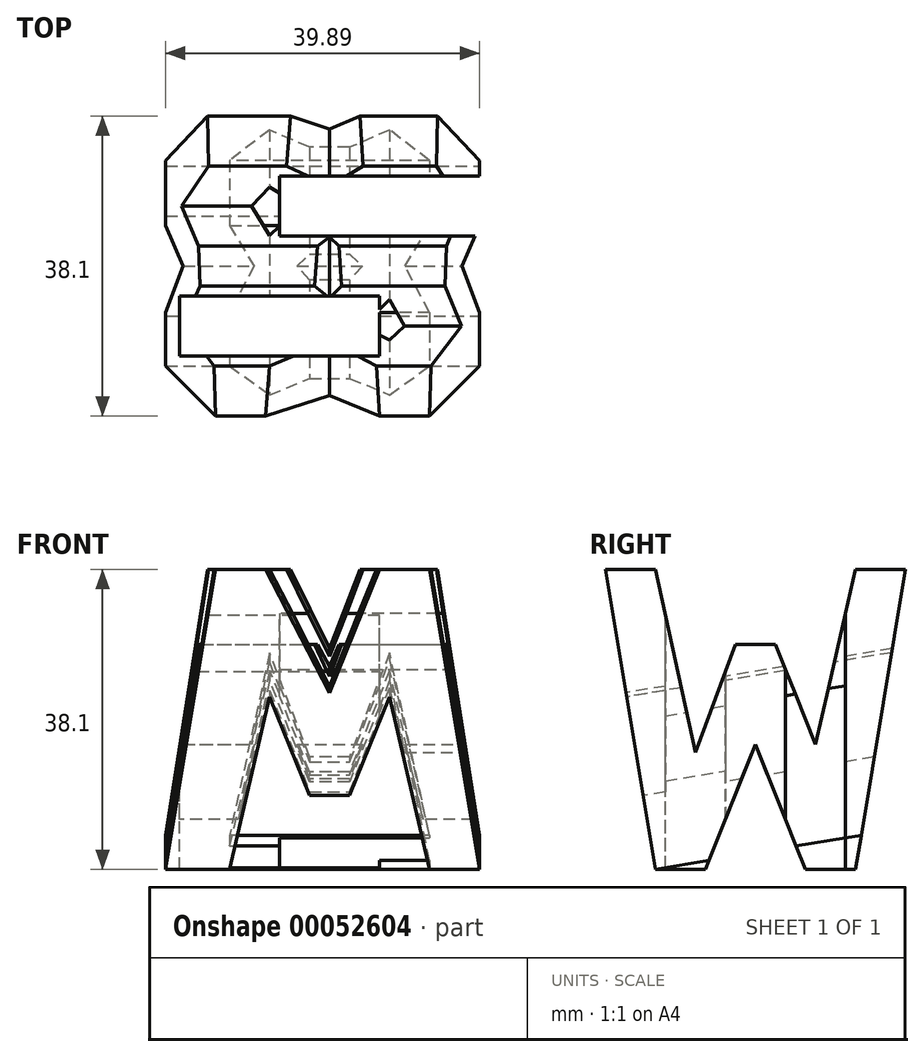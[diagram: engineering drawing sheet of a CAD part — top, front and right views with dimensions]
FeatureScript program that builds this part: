
annotation { "Feature Type Name" : "Feature", "Feature Type Description" : "" }
export const myFeature = defineFeature(function(context is Context, id is Id, definition is map)
    precondition{}
    {
        {
            var Q0;
            Q0=qCreatedBy(makeId("Front.planeOp"),FACE);
            var sketch = newSketch(context, id + "F0", { "sketchPlane" : qUnion([Q0])});
            skLineSegment(sketch, "E0", {"start": v(0, 0) * mm, "end": v(0, 38.1) * mm});
            skLineSegment(sketch, "E1", {"start": v(0, 38.1) * mm, "end": v(-39.89, 38.1) * mm});
            skLineSegment(sketch, "E2", {"start": v(-39.89, 38.1) * mm, "end": v(-39.89, 0) * mm});
            skLineSegment(sketch, "E3", {"start": v(-39.89, 0) * mm, "end": v(0, 0) * mm});
            skSolve(sketch);
        }
        {
            var Q0;
            Q0=makeQuery(id+"F0.imprint","IMPRINT",FACE,{"disambiguationData":[TD([[makeQuery(id+"F0.imprint","IMPRINT",EDGE,{"derivedFrom":sQuery(id+"F0.wireOp",EDGE,"E0")}),1.0]])]});
            extrude(context, id + "F1", {"entities" : qUnion([Q0]), "depth" : 38.1 * mm});
        }
        {
            var Q0;
            Q0=makeQuery(id+"F1.opExtrude","SWEPT_FACE",FACE,{"disambiguationData":[OSD([sQuery(id+"F0.wireOp",EDGE,"E0")])]});
            var sketch = newSketch(context, id + "F2", { "sketchPlane" : qUnion([Q0])});
            skLineSegment(sketch, "E4", {"start": v(-38.1, 38.1) * mm, "end": v(-31.75, 0) * mm});
            skLineSegment(sketch, "E5", {"start": v(-31.75, 0) * mm, "end": v(-25.4, 0) * mm});
            skLineSegment(sketch, "E6", {"start": v(-25.4, 0) * mm, "end": v(-19.05, 15.88) * mm});
            skLineSegment(sketch, "E7", {"start": v(-19.05, 15.88) * mm, "end": v(-12.7, 0) * mm});
            skLineSegment(sketch, "E8", {"start": v(-12.7, 0) * mm, "end": v(-6.35, 0) * mm});
            skLineSegment(sketch, "E9", {"start": v(-6.35, 0) * mm, "end": v(0, 38.1) * mm});
            skLineSegment(sketch, "E10", {"start": v(-6.35, 38.1) * mm, "end": v(-11.43, 15.86) * mm});
            skLineSegment(sketch, "E11", {"start": v(-11.43, 15.86) * mm, "end": v(-16.51, 28.58) * mm});
            skLineSegment(sketch, "E12", {"start": v(-16.51, 28.58) * mm, "end": v(-21.6, 28.58) * mm});
            skLineSegment(sketch, "E13", {"start": v(-21.6, 28.58) * mm, "end": v(-26.67, 14.87) * mm});
            skLineSegment(sketch, "E14", {"start": v(-26.67, 14.87) * mm, "end": v(-31.75, 38.1) * mm});
            skLineSegment(sketch, "E15.bottom", {"start": v(0, 0) * mm, "end": v(-38.1, 0) * mm});
            skLineSegment(sketch, "E15.top", {"start": v(0, 38.1) * mm, "end": v(-38.1, 38.1) * mm});
            skLineSegment(sketch, "E15.left", {"start": v(0, 0) * mm, "end": v(0, 38.1) * mm});
            skLineSegment(sketch, "E15.right", {"start": v(-38.1, 0) * mm, "end": v(-38.1, 38.1) * mm});
            skSolve(sketch);
        }
        {
            var Q0;
            {var subQ0=sQuery(id+"F2.wireOp",EDGE,"E10");Q0=makeQuery(id+"F2.imprint","IMPRINT",FACE,{"disambiguationData":[TD([[makeQuery(id+"F2.imprint","IMPRINT",EDGE,{"derivedFrom":subQ0}),-1.0]])]});}
            var Q1;
            {var subQ0=sQuery(id+"F2.wireOp",EDGE,"E4");Q1=makeQuery(id+"F2.imprint","IMPRINT",FACE,{"disambiguationData":[TD([[makeQuery(id+"F2.imprint","IMPRINT",EDGE,{"derivedFrom":subQ0}),-1.0]])]});}
            var Q2;
            {var subQ0=sQuery(id+"F2.wireOp",EDGE,"E6");Q2=makeQuery(id+"F2.imprint","IMPRINT",FACE,{"disambiguationData":[TD([[makeQuery(id+"F2.imprint","IMPRINT",EDGE,{"derivedFrom":subQ0}),-1.0]])]});}
            var Q3;
            {var subQ0=sQuery(id+"F2.wireOp",EDGE,"E9");Q3=makeQuery(id+"F2.imprint","IMPRINT",FACE,{"disambiguationData":[TD([[makeQuery(id+"F2.imprint","IMPRINT",EDGE,{"derivedFrom":subQ0}),-1.0]])]});}
            extrude(context, id + "F3", {"entities" : qUnion([Q0, Q1, Q2, Q3]), "operationType" : NewBodyOperationType.REMOVE, "oppositeDirection" : true, "depth" : 38.1 * mm});
        }
        {
            var Q0;
            Q0=makeQuery(id+"F3.boolean.opBoolean","COPY",FACE,{"derivedFrom":makeQuery(id+"F3.opExtrude","CAP_FACE",FACE,{"disambiguationData":[OSD([sQuery(id+"F2.wireOp",EDGE,"E10"),sQuery(id+"F2.wireOp",EDGE,"E11"),sQuery(id+"F2.wireOp",EDGE,"E12"),sQuery(id+"F2.wireOp",EDGE,"E13"),sQuery(id+"F2.wireOp",EDGE,"E14"),sQuery(id+"F2.wireOp",EDGE,"E15.top")])],"isStart":false})});
            var Q1;
            Q1=makeQuery(id+"F3.boolean.opBoolean","COPY",FACE,{"derivedFrom":makeQuery(id+"F3.opExtrude","CAP_FACE",FACE,{"disambiguationData":[OSD([sQuery(id+"F2.wireOp",EDGE,"E4"),sQuery(id+"F2.wireOp",EDGE,"E15.bottom"),sQuery(id+"F2.wireOp",EDGE,"E15.right")])],"isStart":false})});
            var Q2;
            Q2=makeQuery(id+"F3.boolean.opBoolean","COPY",FACE,{"derivedFrom":makeQuery(id+"F3.opExtrude","CAP_FACE",FACE,{"disambiguationData":[OSD([sQuery(id+"F2.wireOp",EDGE,"E6"),sQuery(id+"F2.wireOp",EDGE,"E7"),sQuery(id+"F2.wireOp",EDGE,"E15.bottom")])],"isStart":false})});
            var Q3;
            Q3=makeQuery(id+"F3.boolean.opBoolean","COPY",FACE,{"derivedFrom":makeQuery(id+"F3.opExtrude","CAP_FACE",FACE,{"disambiguationData":[OSD([sQuery(id+"F2.wireOp",EDGE,"E9"),sQuery(id+"F2.wireOp",EDGE,"E15.bottom"),sQuery(id+"F2.wireOp",EDGE,"E15.left")])],"isStart":false})});
            extrude(context, id + "F4", {"entities" : qUnion([Q0, Q1, Q2, Q3]), "operationType" : NewBodyOperationType.REMOVE, "oppositeDirection" : true, "depth" : 25.4 * mm});
        }
        {
            var Q0;
            {var subQ0=sQuery(id+"F2.wireOp",EDGE,"E4");Q0=makeQuery(id+"F4.boolean.opBoolean","MERGE",FACE,{"derivedFrom":[makeQuery(id+"F3.boolean.opBoolean","COPY",FACE,{"derivedFrom":makeQuery(id+"F3.opExtrude","SWEPT_FACE",FACE,{"disambiguationData":[OSD([subQ0])]})}),makeQuery(id+"F4.opExtrude","SWEPT_FACE",FACE,{"disambiguationData":[OSD([subQ0])]})]});}
            var sketch = newSketch(context, id + "F5", { "sketchPlane" : qUnion([Q0])});
            skLineSegment(sketch, "E16", {"start": v(-39.89, 5.22) * mm, "end": v(-33.54, 43.85) * mm});
            skLineSegment(sketch, "E17", {"start": v(-33.54, 43.85) * mm, "end": v(-27.19, 43.85) * mm});
            skLineSegment(sketch, "E18", {"start": v(-27.19, 43.85) * mm, "end": v(-19.05, 27.97) * mm});
            skLineSegment(sketch, "E19", {"start": v(-19.05, 27.97) * mm, "end": v(-12.7, 43.85) * mm});
            skLineSegment(sketch, "E20", {"start": v(-12.7, 43.85) * mm, "end": v(-6.35, 43.85) * mm});
            skLineSegment(sketch, "E21", {"start": v(-6.35, 43.85) * mm, "end": v(0, 5.22) * mm});
            skLineSegment(sketch, "E22", {"start": v(-31.75, 5.22) * mm, "end": v(-26.67, 27.44) * mm});
            skLineSegment(sketch, "E23", {"start": v(-26.67, 27.44) * mm, "end": v(-21.6, 14.74) * mm});
            skLineSegment(sketch, "E24", {"start": v(-21.6, 14.74) * mm, "end": v(-16.51, 14.74) * mm});
            skLineSegment(sketch, "E25", {"start": v(-16.51, 14.74) * mm, "end": v(-11.43, 27.44) * mm});
            skLineSegment(sketch, "E26", {"start": v(-11.43, 27.44) * mm, "end": v(-6.35, 5.22) * mm});
            skSolve(sketch);
        }
        {
            var Q0;
            {var subQ0=sQuery(id+"F5.wireOp",EDGE,"E18");Q0=makeQuery(id+"F5.imprint","IMPRINT",FACE,{"disambiguationData":[TD([[makeQuery(id+"F5.imprint","IMPRINT",EDGE,{"derivedFrom":subQ0}),1.0]])]});}
            var Q1;
            {var subQ0=sQuery(id+"F5.wireOp",EDGE,"E16");Q1=makeQuery(id+"F5.imprint","IMPRINT",FACE,{"disambiguationData":[TD([[makeQuery(id+"F5.imprint","IMPRINT",EDGE,{"derivedFrom":subQ0}),1.0]])]});}
            var Q2;
            {var subQ0=sQuery(id+"F5.wireOp",EDGE,"E22");Q2=makeQuery(id+"F5.imprint","IMPRINT",FACE,{"disambiguationData":[TD([[makeQuery(id+"F5.imprint","IMPRINT",EDGE,{"derivedFrom":subQ0}),-1.0]])]});}
            var Q3;
            {var subQ0=sQuery(id+"F5.wireOp",EDGE,"E21");Q3=makeQuery(id+"F5.imprint","IMPRINT",FACE,{"disambiguationData":[TD([[makeQuery(id+"F5.imprint","IMPRINT",EDGE,{"derivedFrom":subQ0}),1.0]])]});}
            extrude(context, id + "F6", {"entities" : qUnion([Q0, Q1, Q2, Q3]), "operationType" : NewBodyOperationType.REMOVE, "oppositeDirection" : true, "depth" : 38.1 * mm});
        }
        {
            var Q0;
            Q0=qCreatedBy(makeId("Top.planeOp"),FACE);
            cPlane(context, id + "F7", {"entities" : qUnion([Q0]), "cplaneType" : CPlaneType.OFFSET, "offset" : 38.1 * mm, "width" : 152.4 * mm, "height" : 152.4 * mm});
        }
        {
            var Q0;
            Q0=qCreatedBy(id+"F7.planeOp",FACE);
            var sketch = newSketch(context, id + "F8", { "sketchPlane" : qUnion([Q0])});
            skLineSegment(sketch, "E27.bottom", {"start": v(0, 0) * mm, "end": v(-38.1, 0) * mm});
            skLineSegment(sketch, "E27.top", {"start": v(0, -38.1) * mm, "end": v(-38.1, -38.1) * mm});
            skLineSegment(sketch, "E27.left", {"start": v(0, 0) * mm, "end": v(0, -38.1) * mm});
            skLineSegment(sketch, "E27.right", {"start": v(-38.1, 0) * mm, "end": v(-38.1, -38.1) * mm});
            skLineSegment(sketch, "E28", {"start": v(0, -7.62) * mm, "end": v(-25.4, -7.62) * mm});
            skLineSegment(sketch, "E29", {"start": v(-25.4, -7.62) * mm, "end": v(-25.4, -15.24) * mm});
            skLineSegment(sketch, "E30", {"start": v(-25.4, -15.24) * mm, "end": v(0, -15.24) * mm});
            skLineSegment(sketch, "E31", {"start": v(-38.1, -22.86) * mm, "end": v(-12.7, -22.86) * mm});
            skLineSegment(sketch, "E32", {"start": v(-12.7, -22.86) * mm, "end": v(-12.7, -30.48) * mm});
            skLineSegment(sketch, "E33", {"start": v(-12.7, -30.48) * mm, "end": v(-38.1, -30.48) * mm});
            skSolve(sketch);
        }
        {
            var Q0;
            {var subQ0=sQuery(id+"F8.wireOp",EDGE,"E28");Q0=makeQuery(id+"F8.imprint","IMPRINT",FACE,{"disambiguationData":[TD([[makeQuery(id+"F8.imprint","IMPRINT",EDGE,{"derivedFrom":subQ0}),1.0]])]});}
            var Q1;
            {var subQ0=sQuery(id+"F8.wireOp",EDGE,"E31");Q1=makeQuery(id+"F8.imprint","IMPRINT",FACE,{"disambiguationData":[TD([[makeQuery(id+"F8.imprint","IMPRINT",EDGE,{"derivedFrom":subQ0}),-1.0]])]});}
            extrude(context, id + "F9", {"entities" : qUnion([Q0, Q1]), "operationType" : NewBodyOperationType.REMOVE, "oppositeDirection" : true, "depth" : 38.1 * mm});
        }
    });
